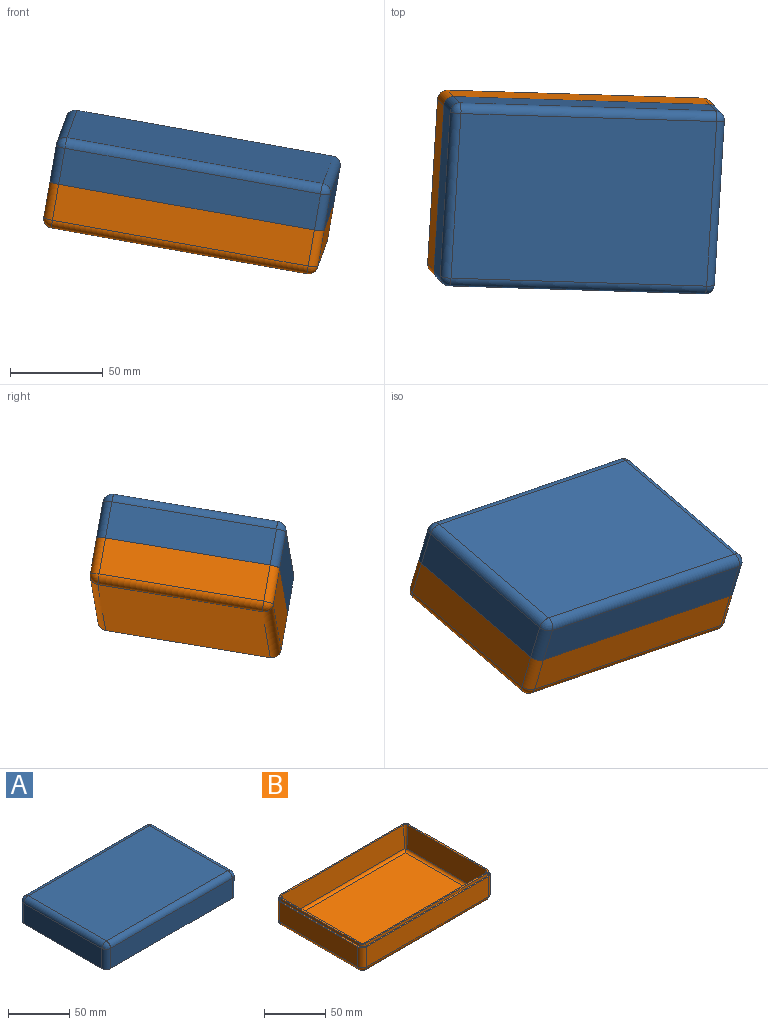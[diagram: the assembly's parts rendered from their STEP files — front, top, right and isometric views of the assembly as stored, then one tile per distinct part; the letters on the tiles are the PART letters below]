
ASSEMBLY  parts=2 mates=1
PART A: 40 faces, bbox 150x100x25 mm
  f0: cylinder r=2.5mm len=91.94mm, axis (0,-1,0), area 343.2mm2, adj f1,f2,f3,f7,f35,f36
  f1: cone r=2.5mm half-angle=3deg, axis (0,0,-1), area 53.5mm2, adj f0,f3,f34,f36,f39
  f2: cone r=2.5mm half-angle=3deg, axis (0,0,-1), area 53.5mm2, adj f0,f7,f34,f36,f37
  f3: cylinder r=2.5mm len=141.94mm, axis (1,0,0), area 533.1mm2, adj f0,f1,f4,f5,f35,f39
  f4: cone r=2.5mm half-angle=3deg, axis (0,0,-1), area 53.5mm2, adj f3,f5,f34,f38,f39
  f5: cylinder r=2.5mm len=91.94mm, axis (0,-1,0), area 343.2mm2, adj f3,f4,f6,f7,f35,f38
  f6: cone r=2.5mm half-angle=3deg, axis (0,0,-1), area 53.5mm2, adj f5,f7,f34,f37,f38
  f7: cylinder r=2.5mm len=141.94mm, axis (1,0,0), area 533.1mm2, adj f0,f2,f5,f6,f35,f37
  f8: plane 150x100mm, normal (0,0,-1), area 609.4mm2, adj f9,f10,f11,f12,f14,f18,f19,f25
  f9: plane 140x20mm, normal (0,1,0), area 2800mm2, adj f8,f19,f22,f25
  f10: plane 90x20mm, normal (-1,0,0), area 1800mm2, adj f8,f18,f23,f25
  f11: plane 140x20mm, normal (0,-1,0), area 2800mm2, adj f8,f14,f17,f18
  f12: plane 90x20mm, normal (1,0,0), area 1800mm2, adj f8,f14,f16,f19
  f13: plane 140x90mm, normal (0,0,1), area 12600mm2, adj f16,f17,f22,f23
  f14: cylinder r=5mm len=20mm, axis (0,0,1), area 157.1mm2, adj f8,f11,f12,f15
  f15: sphere r=5mm, area 39.3mm2, adj f14,f16,f17
  f16: cylinder r=5mm len=90mm, axis (0,-1,0), area 706.9mm2, adj f12,f13,f15,f20
  f17: cylinder r=5mm len=140mm, axis (-1,0,0), area 1099.6mm2, adj f11,f13,f15,f21
  f18: cylinder r=5mm len=20mm, axis (0,0,-1), area 157.1mm2, adj f8,f10,f11,f21
  f19: cylinder r=5mm len=20mm, axis (0,0,-1), area 157.1mm2, adj f8,f9,f12,f20
  f20: sphere r=5mm, area 39.3mm2, adj f16,f19,f22
  f21: sphere r=5mm, area 39.3mm2, adj f17,f18,f23
  f22: cylinder r=5mm len=140mm, axis (1,0,0), area 1099.6mm2, adj f9,f13,f20,f24
  f23: cylinder r=5mm len=90mm, axis (0,1,0), area 706.9mm2, adj f10,f13,f21,f24
  f24: sphere r=5mm, area 39.3mm2, adj f22,f23,f25
  f25: cylinder r=5mm len=20mm, axis (0,0,1), area 157.1mm2, adj f8,f9,f10,f24
  f26: cylinder r=3.75mm len=3.75mm, axis (0,0,1), area 16.2mm2, adj f8,f27,f33,f34
  f27: plane 90x2.75mm, normal (1,0,0), area 247.5mm2, adj f8,f26,f28,f34
  f28: cylinder r=3.75mm len=3.75mm, axis (0,0,1), area 16.2mm2, adj f8,f27,f29,f34
  f29: plane 140x2.75mm, normal (0,-1,0), area 385mm2, adj f8,f28,f30,f34
  f30: cylinder r=3.75mm len=3.75mm, axis (0,0,1), area 16.2mm2, adj f8,f29,f31,f34
  f31: plane 90x2.75mm, normal (-1,0,0), area 247.5mm2, adj f8,f30,f32,f34
  f32: cylinder r=3.75mm len=3.75mm, axis (0,0,1), area 16.2mm2, adj f8,f31,f33,f34
  f33: plane 140x2.75mm, normal (0,1,0), area 385mm2, adj f8,f26,f32,f34
  f34: plane 147.5x97.5mm, normal (0,0,-1), area 668mm2, adj f1,f2,f4,f6,f26,f27,f28,f29
  f35: plane 137.9x87.9mm, normal (0,0,-1), area 12120.7mm2, adj f0,f3,f5,f7
  f36: plane 90x17.38mm, normal (-1,0,-0.05), area 1566.4mm2, adj f0,f1,f2,f34
  f37: plane 140x17.38mm, normal (0,1,-0.05), area 2436.7mm2, adj f2,f6,f7,f34
  f38: plane 90x17.38mm, normal (1,0,-0.05), area 1566.4mm2, adj f4,f5,f6,f34
  f39: plane 140x17.38mm, normal (0,-1,-0.05), area 2436.7mm2, adj f1,f3,f4,f34
PART B: 40 faces, bbox 150x100x27.8 mm
  f0: cylinder r=2.5mm len=91.75mm, axis (0,1,0), area 342.5mm2, adj f1,f2,f3,f7,f35,f39
  f1: cone r=2.5mm half-angle=3deg, axis (0,0,1), area 69.7mm2, adj f0,f7,f34,f38,f39
  f2: cone r=2.5mm half-angle=3deg, axis (0,0,1), area 69.7mm2, adj f0,f3,f34,f36,f39
  f3: cylinder r=2.5mm len=141.75mm, axis (-1,0,0), area 532.3mm2, adj f0,f2,f4,f5,f35,f36
  f4: cone r=2.5mm half-angle=3deg, axis (0,0,1), area 69.7mm2, adj f3,f5,f34,f36,f37
  f5: cylinder r=2.5mm len=91.75mm, axis (0,1,0), area 342.5mm2, adj f3,f4,f6,f7,f35,f37
  f6: cone r=2.5mm half-angle=3deg, axis (0,0,1), area 69.7mm2, adj f5,f7,f34,f37,f38
  f7: cylinder r=2.5mm len=141.75mm, axis (-1,0,0), area 532.3mm2, adj f0,f1,f5,f6,f35,f38
  f8: plane 150x100mm, normal (0,0,1), area 609.4mm2, adj f18,f19,f20,f21,f22,f23,f24,f25
  f9: plane 140x90mm, normal (0,0,-1), area 12600mm2, adj f10,f11,f12,f13
  f10: cylinder r=5mm len=140mm, axis (-1,0,0), area 1099.6mm2, adj f9,f16,f17,f25
  f11: cylinder r=5mm len=90mm, axis (0,-1,0), area 706.9mm2, adj f9,f15,f17,f24
  f12: cylinder r=5mm len=140mm, axis (1,0,0), area 1099.6mm2, adj f9,f14,f15,f22
  f13: cylinder r=5mm len=90mm, axis (0,1,0), area 706.9mm2, adj f9,f14,f16,f20
  f14: sphere r=5mm, area 39.3mm2, adj f12,f13,f18
  f15: sphere r=5mm, area 39.3mm2, adj f11,f12,f21
  f16: sphere r=5mm, area 39.3mm2, adj f10,f13,f19
  f17: sphere r=5mm, area 39.3mm2, adj f10,f11,f23
  f18: cylinder r=5mm len=20mm, axis (0,0,1), area 157.1mm2, adj f8,f14,f20,f22
  f19: cylinder r=5mm len=20mm, axis (0,0,-1), area 157.1mm2, adj f8,f16,f20,f25
  f20: plane 90x20mm, normal (1,0,0), area 1800mm2, adj f8,f13,f18,f19
  f21: cylinder r=5mm len=20mm, axis (0,0,-1), area 157.1mm2, adj f8,f15,f22,f24
  f22: plane 140x20mm, normal (0,-1,0), area 2800mm2, adj f8,f12,f18,f21
  f23: cylinder r=5mm len=20mm, axis (0,0,1), area 157.1mm2, adj f8,f17,f24,f25
  f24: plane 90x20mm, normal (-1,0,0), area 1800mm2, adj f8,f11,f21,f23
  f25: plane 140x20mm, normal (0,1,0), area 2800mm2, adj f8,f10,f19,f23
  f26: cylinder r=3.75mm len=3.75mm, axis (0,0,1), area 16.2mm2, adj f8,f27,f33,f34
  f27: plane 90x2.75mm, normal (-1,0,0), area 247.5mm2, adj f8,f26,f28,f34
  f28: cylinder r=3.75mm len=3.75mm, axis (0,0,1), area 16.2mm2, adj f8,f27,f29,f34
  f29: plane 140x2.75mm, normal (0,1,0), area 385mm2, adj f8,f28,f30,f34
  f30: cylinder r=3.75mm len=3.75mm, axis (0,0,1), area 16.2mm2, adj f8,f29,f31,f34
  f31: plane 90x2.75mm, normal (1,0,0), area 247.5mm2, adj f8,f30,f32,f34
  f32: cylinder r=3.75mm len=3.75mm, axis (0,0,1), area 16.2mm2, adj f8,f31,f33,f34
  f33: plane 140x2.75mm, normal (0,-1,0), area 385mm2, adj f8,f26,f32,f34
  f34: plane 147.5x97.5mm, normal (0,0,1), area 599.5mm2, adj f1,f2,f4,f6,f26,f27,f28,f29
  f35: plane 137.61x87.61mm, normal (0,0,1), area 12055.7mm2, adj f0,f3,f5,f7
  f36: plane 140x22.88mm, normal (0,-1,0.05), area 3207.7mm2, adj f2,f3,f4,f34
  f37: plane 90x22.88mm, normal (1,0,0.05), area 2062.1mm2, adj f4,f5,f6,f34
  f38: plane 140x22.88mm, normal (0,1,0.05), area 3207.7mm2, adj f1,f6,f7,f34
  f39: plane 90x22.88mm, normal (-1,0,0.05), area 2062.1mm2, adj f0,f1,f2,f34
PLACE A rot(axis=(0.68,0.71,-0.18),14.1deg) t=(-36.93,-52.31,-108.9)mm
PLACE B rot(axis=(0.68,0.71,-0.18),14.1deg) t=(-36.93,-52.31,-108.9)mm
MATE fastened B.f27 <-> A.f27  axis (-0.98,0.03,0.18) through (-109.26,-50.32,-94.57)mm
